# Revit family: Showerhead-American_Standard-HydroFocus-1660509_Series
name_source: partatom
category: Plumbing Fixtures
units: mm (PartAtom-declared; Revit-internal decimal feet)

## family parameters
Always vertical = No
Cut with Voids When Loaded = No
OmniClass Number = 23.45.05.14.17
OmniClass Title = Showers
Part Type = Normal
Room Calculation Point = No
Round Connector Dimension = Use Diameter
Shared = Yes
Work Plane-Based = Yes

## types (5) — shared parameters
1660.240 - Standard Shower Arm and Flange = No
1660.241 - Modern Shower Arm and Flange = No
Assembly Code = D2010710
CEC Compliant = Yes
CW Connection = No
CWFU = 3
CalGreen Compliant = Yes
Default Elevation = 0"
Description = Townsend® 6-Inch 1.8 gpm/6.8 L/min Water-Saving Fixed Showerhead
Flow Rate = 1.75 gpm (6.8 L/min)
HW Connection = No
HWFU = 3
Height = 2 5/8"
IAPMO Compliance = These products meet or exceed the following codes and standards: ASME A112.18.1,CSA B125.1
Length = 6 1/8"
Manufacturer = American Standard
Price = Prices may vary. Please consult Manufacturer Representative for most up-to-date price list.
Product Page URL = https://www.americanstandard-us.com
Revised Date = 11/17/2022
Tempered Water Connection = Yes
Tempered Water Connection Diameter = 1/2"
Tempered Water Connection Radius = 1/4"
URL = https://www.americanstandard-us.com
Vent Connection = No
WFU = 4
Warranty Information = One Year General Product Warranty
Waste Connection = No
Width = 6 1/8"

## per-type parameters (varying)
| type | Finish | Material | Model | Product Documentation Link |
| 1660509.002 | Brass-American Standard-002-Polished Chrome | Brass-American Standard-002-Polished Chrome | 1660509.002 | https://americanstandard.box.com |
| 1660509.013 | Brass-American Standard-013-Polished Nickel | Brass-American Standard-013-Polished Nickel | 1660509.013 | https://americanstandard.box.com |
| 1660509.295 | Brass-American Standard-295-Brushed Nickel | Brass-American Standard-295-Brushed Nickel | 1660509.295 | https:https://americanstandard.box.com |
| 1660509.278 | Brass-American Standard-278-Legacy Bronze | Brass-American Standard-278-Legacy Bronze | 1660509 | https://americanstandard.box.com |
| 1660509.243 | Brass-American Standard-278-Legacy Bronze | Brass-American Standard-278-Legacy Bronze | 1660509.243 | https://americanstandard.box.com |

## geometry (parser evidence)
native form markers: Sweep x2
no freeform markers — native parametric forms only
